# Revit family: Firestop-Putty-STI-Putty_Pads-Right_Side_of_Stud
name_source: partatom
category: Specialty Equipment
units: mm (PartAtom-declared; Revit-internal decimal feet)

## family parameters
Always vertical = Yes
Classification Number = 23.20.50.14
Cut with Voids When Loaded = No
Enable Cutting in Views = No
Host = Wall
Maintain Annotation Orientation = No
Part Type = Normal
Room Calculation Point = No
Round Connector Dimension = Use Diameter
Shared = No

## types (1)
- EP23, EP24, EP44 & EP45
    Assembly Code = D4030900
    Color (Standard) = Red
    Default Elevation = 0' - 0"
    Description = SpecSeal® Series SSP Intumescent Firestop Putty
    Fire Rating = Up to 2 Hr
    Firestopping Intumescent = STI-Molded-Intumescent
    Green Building/LEED® Information = http://sti.fmpdata.net
    Guide Specification = http://www.stifirestop.com
    Locate Distributor = http://www.stifirestop.com
    MSDS = http://files.systems.stifirestop.com
    Manufacturer = Specified Technologies Inc.
    Manufacturer Fax No. = 908.526.9623
    Model = EP23, EP24, EP44 & EP45
    Product Documentation Link = http://sti.fmpdata.net
    Product Page URL = http://www.stifirestop.com
    Tested Systems = http://sti.fmpdata.net
    URL = http://www.stifirestop.com

## geometry (parser evidence)
native form markers: Sweep x3
no freeform markers — native parametric forms only
